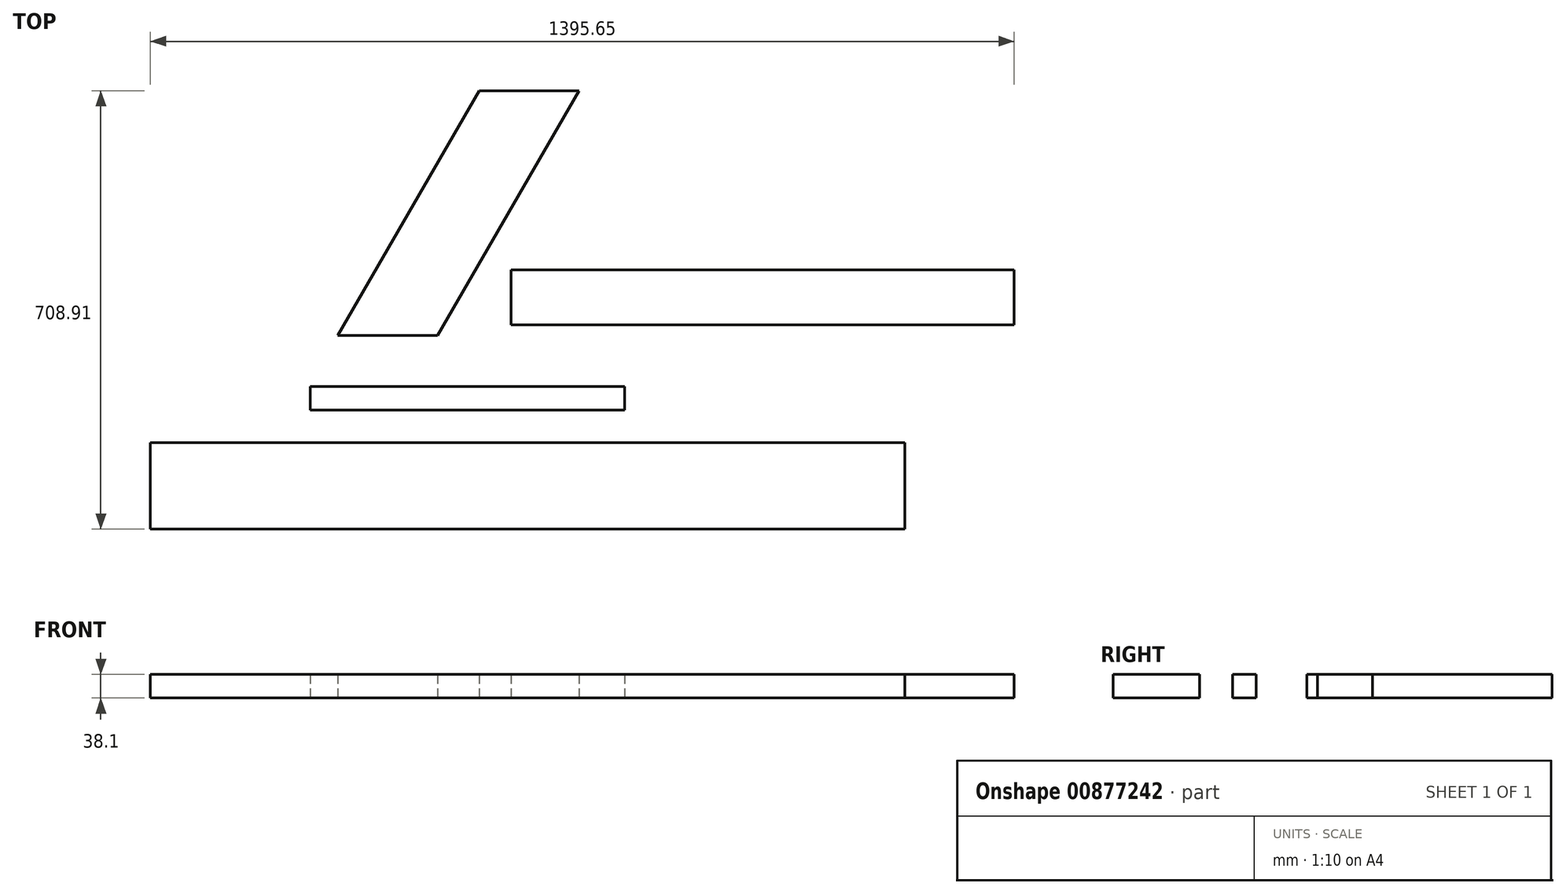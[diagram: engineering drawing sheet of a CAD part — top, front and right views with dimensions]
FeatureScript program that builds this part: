
annotation { "Feature Type Name" : "Feature", "Feature Type Description" : "" }
export const myFeature = defineFeature(function(context is Context, id is Id, definition is map)
    precondition{}
    {
        {
            var Q0;
            Q0=qCreatedBy(makeId("Top.planeOp"),FACE);
            var sketch = newSketch(context, id + "F0", { "sketchPlane" : qUnion([Q0])});
            skLineSegment(sketch, "E0.bottom", {"start": v(594.42, -166.46) * mm, "end": v(-624.78, -166.46) * mm});
            skLineSegment(sketch, "E0.top", {"start": v(594.42, -26.76) * mm, "end": v(-624.78, -26.76) * mm});
            skLineSegment(sketch, "E0.left", {"start": v(594.42, -166.46) * mm, "end": v(594.42, -26.76) * mm});
            skLineSegment(sketch, "E0.right", {"start": v(-624.78, -166.46) * mm, "end": v(-624.78, -26.76) * mm});
            skLineSegment(sketch, "E1", {"start": v(-421.58, -166.46) * mm, "end": v(-421.58, -26.76) * mm, "construction": true});
            skLineSegment(sketch, "E2", {"start": v(391.22, -26.76) * mm, "end": v(391.22, -166.46) * mm, "construction": true});
            skSolve(sketch);
        }
        {
            var Q0;
            Q0=makeQuery(id+"F0.imprint","IMPRINT",FACE,{"disambiguationData":[TD([[makeQuery(id+"F0.imprint","IMPRINT",EDGE,{"derivedFrom":sQuery(id+"F0.wireOp",EDGE,"E0.bottom")}),-1.0]])]});
            extrude(context, id + "F1", {"entities" : qUnion([Q0]), "depth" : 38.1 * mm, "offsetDistance" : 25.4 * mm});
        }
        {
            var Q0;
            Q0=qCreatedBy(makeId("Top.planeOp"),FACE);
            var sketch = newSketch(context, id + "F2", { "sketchPlane" : qUnion([Q0])});
            skLineSegment(sketch, "E3.bottom", {"start": v(-366.54, 64.28) * mm, "end": v(141.46, 64.28) * mm});
            skLineSegment(sketch, "E3.top", {"start": v(-366.54, 26.18) * mm, "end": v(141.46, 26.18) * mm});
            skLineSegment(sketch, "E3.left", {"start": v(-366.54, 64.28) * mm, "end": v(-366.54, 26.18) * mm});
            skLineSegment(sketch, "E3.right", {"start": v(141.46, 64.28) * mm, "end": v(141.46, 26.18) * mm});
            skSolve(sketch);
        }
        {
            var Q0;
            Q0 = qSketchRegion(id + "F2", true);
            extrude(context, id + "F3", {"entities" : qUnion([Q0]), "depth" : 38.1 * mm, "offsetDistance" : 25.4 * mm});
        }
        {
            var Q0;
            Q0=qCreatedBy(makeId("Top.planeOp"),FACE);
            var sketch = newSketch(context, id + "F4", { "sketchPlane" : qUnion([Q0])});
            skLineSegment(sketch, "E4", {"start": v(-322.13, 146.5) * mm, "end": v(-160.82, 146.5) * mm});
            skLineSegment(sketch, "E5", {"start": v(-160.82, 146.5) * mm, "end": v(67.78, 542.45) * mm});
            skLineSegment(sketch, "E6", {"start": v(67.78, 542.45) * mm, "end": v(-93.53, 542.45) * mm});
            skLineSegment(sketch, "E7", {"start": v(-93.53, 542.45) * mm, "end": v(-322.13, 146.5) * mm});
            skSolve(sketch);
        }
        {
            var Q0;
            Q0 = qSketchRegion(id + "F4", true);
            extrude(context, id + "F5", {"entities" : qUnion([Q0]), "depth" : 38.1 * mm, "offsetDistance" : 25.4 * mm});
        }
        {
            var Q0;
            Q0=qCreatedBy(makeId("Top.planeOp"),FACE);
            var sketch = newSketch(context, id + "F6", { "sketchPlane" : qUnion([Q0])});
            skLineSegment(sketch, "E8.bottom", {"start": v(-41.93, 252.68) * mm, "end": v(770.87, 252.68) * mm});
            skLineSegment(sketch, "E8.top", {"start": v(-41.93, 163.78) * mm, "end": v(770.87, 163.78) * mm});
            skLineSegment(sketch, "E8.left", {"start": v(-41.93, 252.68) * mm, "end": v(-41.93, 163.78) * mm});
            skLineSegment(sketch, "E8.right", {"start": v(770.87, 252.68) * mm, "end": v(770.87, 163.78) * mm});
            skSolve(sketch);
        }
        {
            var Q0;
            Q0 = qSketchRegion(id + "F6", true);
            extrude(context, id + "F7", {"entities" : qUnion([Q0]), "depth" : 38.1 * mm, "offsetDistance" : 25.4 * mm});
        }
    });
